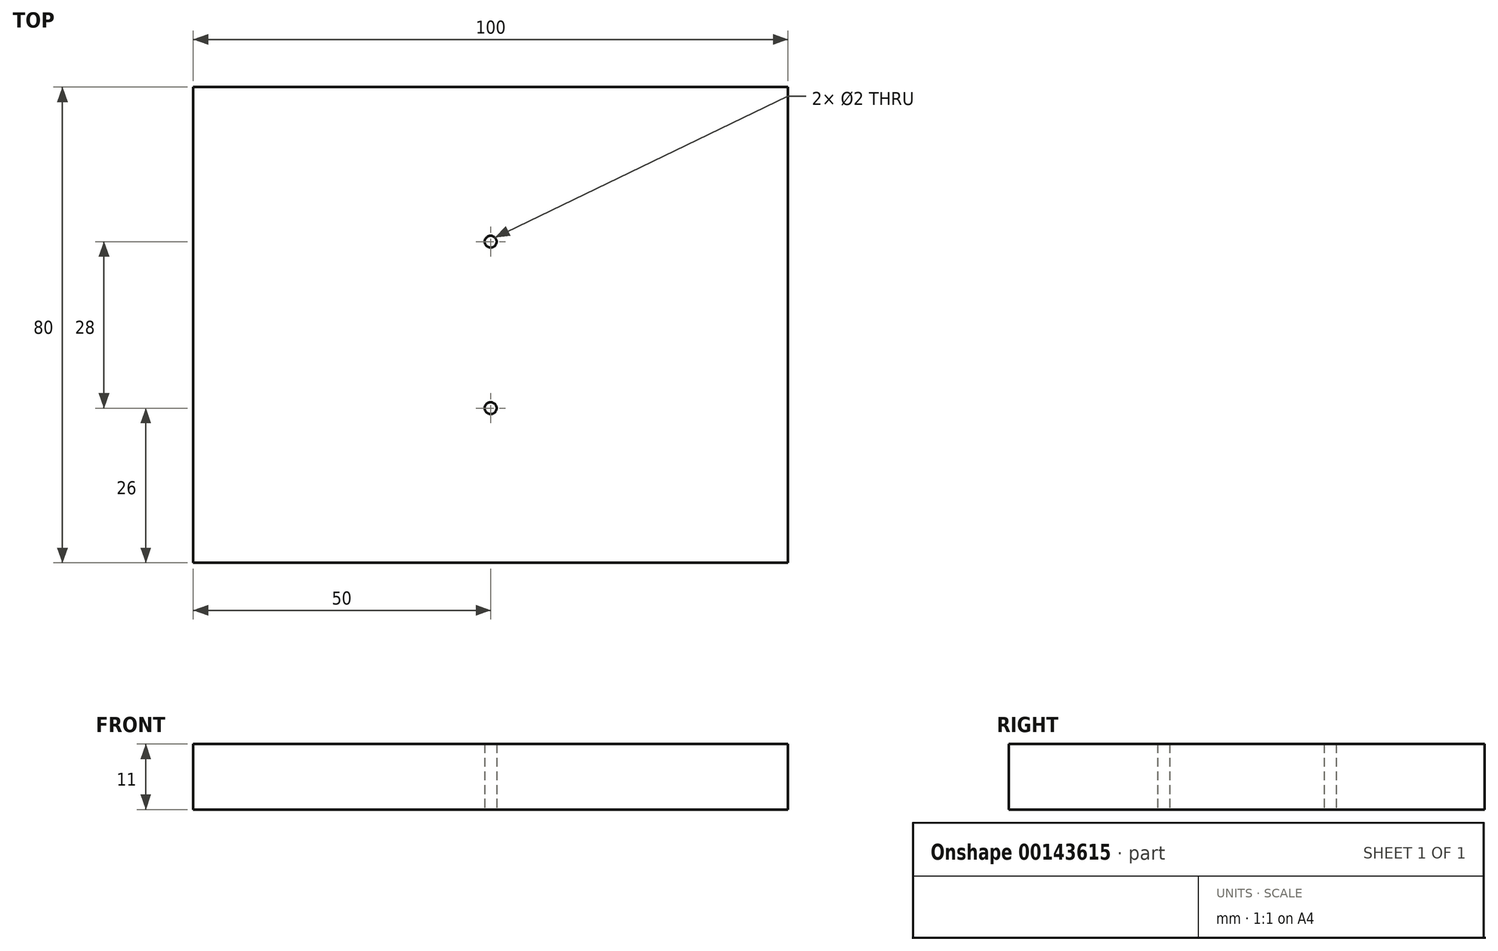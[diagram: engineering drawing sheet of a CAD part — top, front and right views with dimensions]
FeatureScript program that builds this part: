
annotation { "Feature Type Name" : "Feature", "Feature Type Description" : "" }
export const myFeature = defineFeature(function(context is Context, id is Id, definition is map)
    precondition{}
    {
        {
            var Q0;
            Q0=qCreatedBy(makeId("Top.planeOp"),FACE);
            var sketch = newSketch(context, id + "F0", { "sketchPlane" : qUnion([Q0])});
            skLineSegment(sketch, "E0.bottom", {"start": v(50, -40) * mm, "end": v(-50, -40) * mm});
            skLineSegment(sketch, "E0.top", {"start": v(50, 40) * mm, "end": v(-50, 40) * mm});
            skLineSegment(sketch, "E0.left", {"start": v(50, -40) * mm, "end": v(50, 40) * mm});
            skLineSegment(sketch, "E0.right", {"start": v(-50, -40) * mm, "end": v(-50, 40) * mm});
            skPoint(sketch, "E0.middle", {"position": v(0, 0) * mm});
            skLineSegment(sketch, "E1", {"start": v(0, 0) * mm, "end": v(16.46, 0) * mm, "construction": true});
            skCircle(sketch, "E2", {"center": v(0, 14) * mm, "radius": 1 * mm});
            skCircle(sketch, "E3.MirrorC", {"center": v(0, -14) * mm, "radius": 1 * mm});
            skSolve(sketch);
        }
        {
            var Q0;
            Q0 = qSketchRegion(id + "F0", true);
            extrude(context, id + "F1", {"entities" : qUnion([Q0]), "depth" : 11 * mm});
        }
    });
